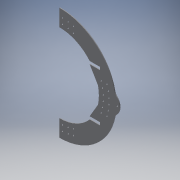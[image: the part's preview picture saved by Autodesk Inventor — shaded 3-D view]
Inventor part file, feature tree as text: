
AUTODESK INVENTOR PART (.ipt)
format: ipt  version: 2016 (Build 200138000, 138)  size: 445,952 bytes
history: native  units: in
note: dims shown in document units (in); Inventor stores cm internally (conversion verified against a paired STEP export)
features: extrude x7, sketch x7, reference x5, projected_geometry x5, plane x1
ambient origin geometry x8: Origin, YZ Plane, XZ Plane, XY Plane, X Axis, Y Axis, Z Axis, Center Point
bodies: Solid1 (feature_tree)
feature tree (25):
  extrude  "Extrusion1"  Depth=0.26in
  extrude  "Extrusion2"  Depth=0.5in
  extrude  "Extrusion3"  Depth=1.0in TaperAngle=0.0deg
  extrude  "Extrusion4"  Depth=0.125in TaperAngle=0.0deg
  plane  "Work Plane1"
  extrude  "Extrusion5"  Depth=0.26in
  extrude  "Extrusion6"  Depth=0.26in
  extrude  "Extrusion7"  Depth=0.125in
  sketch  "Sketch1"  dims[d0=20.0in d3=0.26in]
  reference  "Reference1"
  reference  "Reference2"
  sketch  "Sketch2"  dims[d7=0.26in d8=0.5in]
  projected_geometry  "Projected Loop1"
  sketch  "Sketch3"  dims[d9=0.125in d10=0.0in d11=1.0in d12=0.0in]
  projected_geometry  "Projected Loop2"
  sketch  "Sketch4"  dims[d13=1.0in d14=0.125in d15=0.0in]
  projected_geometry  "Projected Loop3"
  sketch  "Sketch5"  dims[d19=0.26in d20=0.26in]
  reference  "Reference3"
  sketch  "Sketch8"  dims[d21=0.26in d22=0.26in]
  projected_geometry  "Projected Loop5"
  sketch  "Sketch9"  dims[d23=0.26in d24=0.26in d25=0.26in d26=0.26in d27=0.26in d28=0.26in d29=0.26in d30=0.26in d31=0.26in d32=0.26in d33=0.26in d34=0.26in d35=0.26in d36=0.26in d37=0.26in d38=0.26in d39=0.26in d40=0.26in d41=0.26in d42=0.26in d43=0.125in d44=0.0in d45=0.5in d46=0.0in d47=1.0in d48=0.0in d49=2.5in d50=2.5in d51=0.125in d52=0.0in]
  projected_geometry  "Projected Loop6"
  reference  "Reference4"
  reference  "Reference5"
